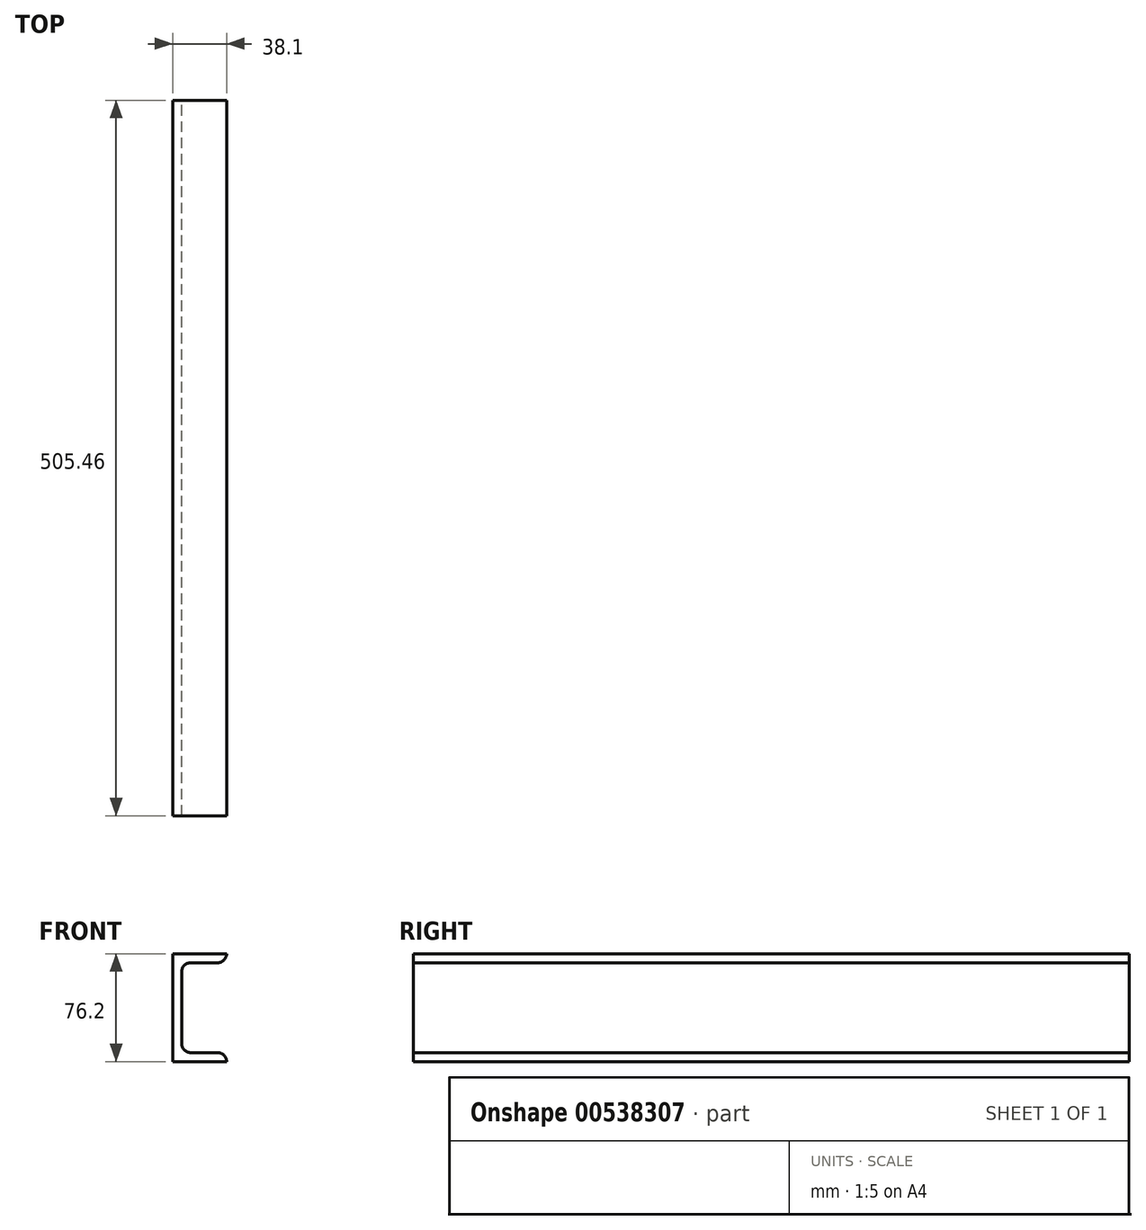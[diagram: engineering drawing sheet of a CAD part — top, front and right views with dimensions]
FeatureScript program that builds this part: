
annotation { "Feature Type Name" : "Feature", "Feature Type Description" : "" }
export const myFeature = defineFeature(function(context is Context, id is Id, definition is map)
    precondition{}
    {
        {
            var Q0;
            Q0=qCreatedBy(makeId("Front.planeOp"),FACE);
            var sketch = newSketch(context, id + "F0", { "sketchPlane" : qUnion([Q0])});
            skLineSegment(sketch, "E0", {"start": v(0, 0) * mm, "end": v(0, 76.2) * mm});
            skLineSegment(sketch, "E1", {"start": v(0, 76.2) * mm, "end": v(38.1, 76.2) * mm});
            skLineSegment(sketch, "E2", {"start": v(0, 0) * mm, "end": v(38.1, 0) * mm});
            skLineSegment(sketch, "E3.0", {"start": v(12.7, 69.85) * mm, "end": v(31.75, 69.85) * mm});
            skLineSegment(sketch, "E3.1", {"start": v(6.35, 12.7) * mm, "end": v(6.35, 63.5) * mm});
            skLineSegment(sketch, "E3.2", {"start": v(12.7, 6.35) * mm, "end": v(31.75, 6.35) * mm});
            skLineSegment(sketch, "E4", {"start": v(38.1, 76.2) * mm, "end": v(38.1, 76.2) * mm});
            skLineSegment(sketch, "E5", {"start": v(38.1, 0) * mm, "end": v(38.1, 0) * mm});
            skPoint(sketch, "E6.visualSharp", {"position": v(38.1, 69.85) * mm});
            skArc(sketch, "E6.filletArc", {"start": v(31.75, 69.85) * mm, "mid": v(36.24, 71.7) * mm, "end": v(38.1, 76.2) * mm});
            skPoint(sketch, "E7.visualSharp", {"position": v(6.35, 69.85) * mm});
            skArc(sketch, "E7.filletArc", {"start": v(12.7, 69.85) * mm, "mid": v(8.2, 68) * mm, "end": v(6.35, 63.5) * mm});
            skPoint(sketch, "E8.visualSharp", {"position": v(6.35, 6.35) * mm});
            skArc(sketch, "E8.filletArc", {"start": v(6.35, 12.7) * mm, "mid": v(8.2, 8.2) * mm, "end": v(12.7, 6.35) * mm});
            skPoint(sketch, "E9.visualSharp", {"position": v(38.1, 6.35) * mm});
            skArc(sketch, "E9.filletArc", {"start": v(38.1, 0) * mm, "mid": v(36.24, 4.5) * mm, "end": v(31.75, 6.35) * mm});
            skSolve(sketch);
        }
        {
            var Q0;
            Q0 = qSketchRegion(id + "F0", true);
            extrude(context, id + "F1", {"entities" : qUnion([Q0]), "depth" : 505.46 * mm, "offsetDistance" : 25.4 * mm});
        }
    });
